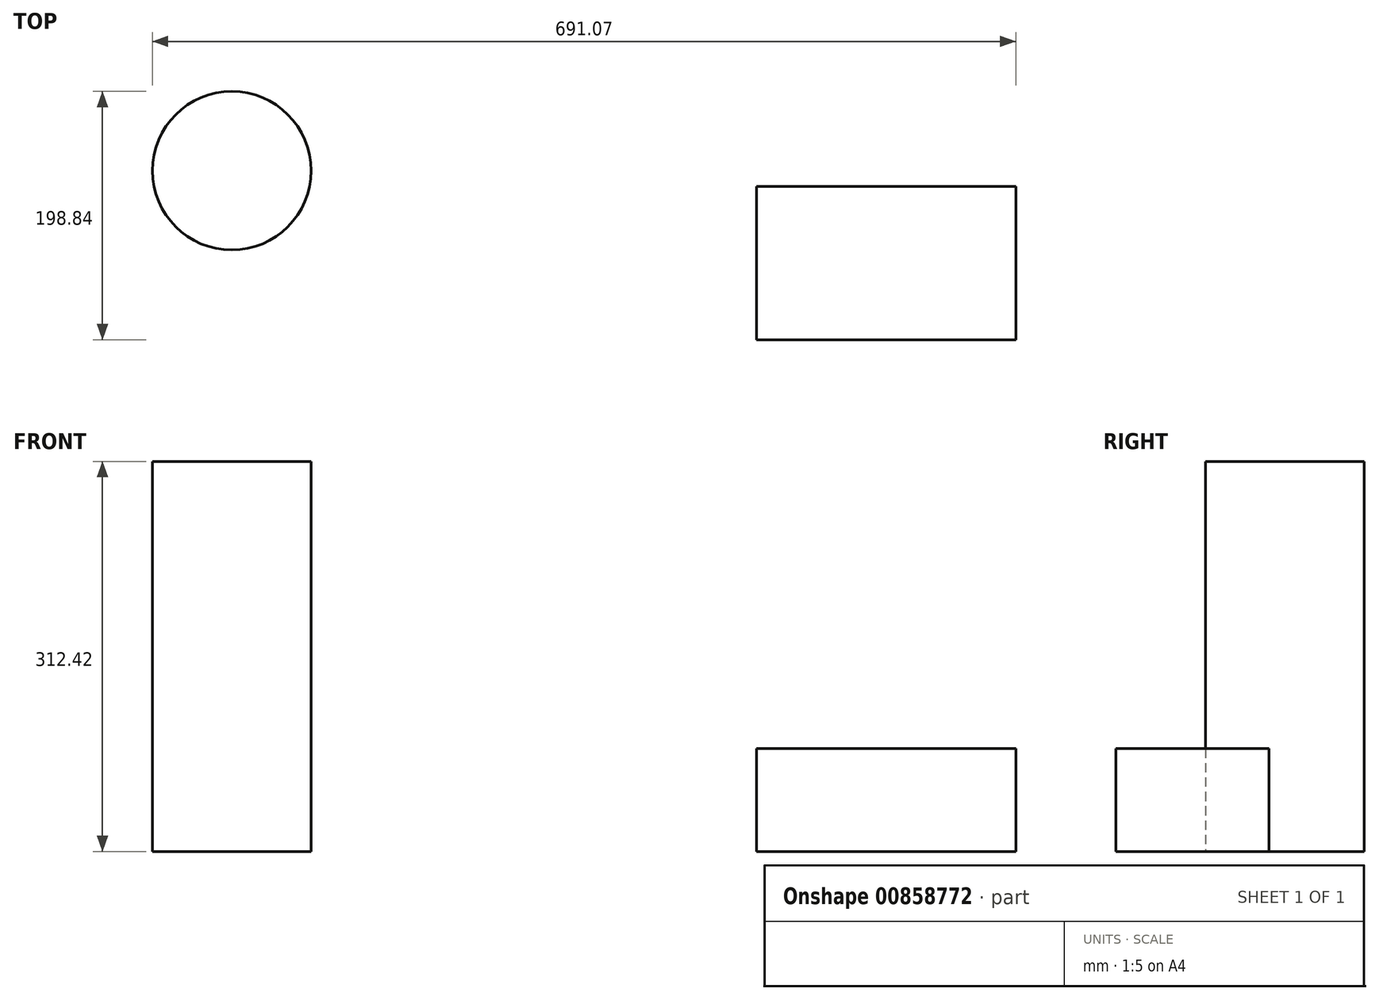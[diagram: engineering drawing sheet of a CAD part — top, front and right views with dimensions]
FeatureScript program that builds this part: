
annotation { "Feature Type Name" : "Feature", "Feature Type Description" : "" }
export const myFeature = defineFeature(function(context is Context, id is Id, definition is map)
    precondition{}
    {
        {
            var Q0;
            Q0=qCreatedBy(makeId("Top.planeOp"),FACE);
            var sketch = newSketch(context, id + "F0", { "sketchPlane" : qUnion([Q0])});
            skCircle(sketch, "E0", {"center": v(-311.54, 245.35) * mm, "radius": 63.5 * mm});
            skLineSegment(sketch, "E1.bottom", {"start": v(108.5, 232.64) * mm, "end": v(316.03, 232.64) * mm});
            skLineSegment(sketch, "E1.top", {"start": v(108.5, 110) * mm, "end": v(316.03, 110) * mm});
            skLineSegment(sketch, "E1.left", {"start": v(108.5, 232.64) * mm, "end": v(108.5, 110) * mm});
            skLineSegment(sketch, "E1.right", {"start": v(316.03, 232.64) * mm, "end": v(316.03, 110) * mm});
            skLineSegment(sketch, "E2", {"start": v(-335.96, -77.57) * mm, "end": v(-142.58, -143.6) * mm});
            skLineSegment(sketch, "E3", {"start": v(-142.58, -143.6) * mm, "end": v(-142.58, -336.98) * mm});
            skLineSegment(sketch, "E4", {"start": v(-142.58, -336.98) * mm, "end": v(-364.26, -372.36) * mm});
            skLineSegment(sketch, "E5", {"start": v(-364.26, -372.36) * mm, "end": v(-335.96, -77.57) * mm});
            skLineSegment(sketch, "E6", {"start": v(-277, -160.1) * mm, "end": v(-310.02, -292.17) * mm});
            skLineSegment(sketch, "E7", {"start": v(-310.02, -292.17) * mm, "end": v(-239, -309.93) * mm});
            skLineSegment(sketch, "E8", {"start": v(-239, -309.93) * mm, "end": v(-277, -160.1) * mm});
            skSolve(sketch);
        }
        {
            var Q0;
            Q0=makeQuery(id+"F0.imprint","IMPRINT",FACE,{"disambiguationData":[TD([[makeQuery(id+"F0.imprint","IMPRINT",EDGE,{"derivedFrom":sQuery(id+"F0.wireOp",EDGE,"E1.bottom")}),-1.0]])]});
            extrude(context, id + "F1", {"entities" : qUnion([Q0]), "depth" : 82.3 * mm, "offsetDistance" : 25.4 * mm});
        }
        {
            var Q0;
            Q0=makeQuery(id+"F0.imprint","IMPRINT",FACE,{"disambiguationData":[TD([[makeQuery(id+"F0.imprint","IMPRINT",EDGE,{"derivedFrom":sQuery(id+"F0.wireOp",EDGE,"E0")}),1.0]])]});
            extrude(context, id + "F2", {"entities" : qUnion([Q0]), "depth" : 312.42 * mm, "offsetDistance" : 25.4 * mm});
        }
    });
